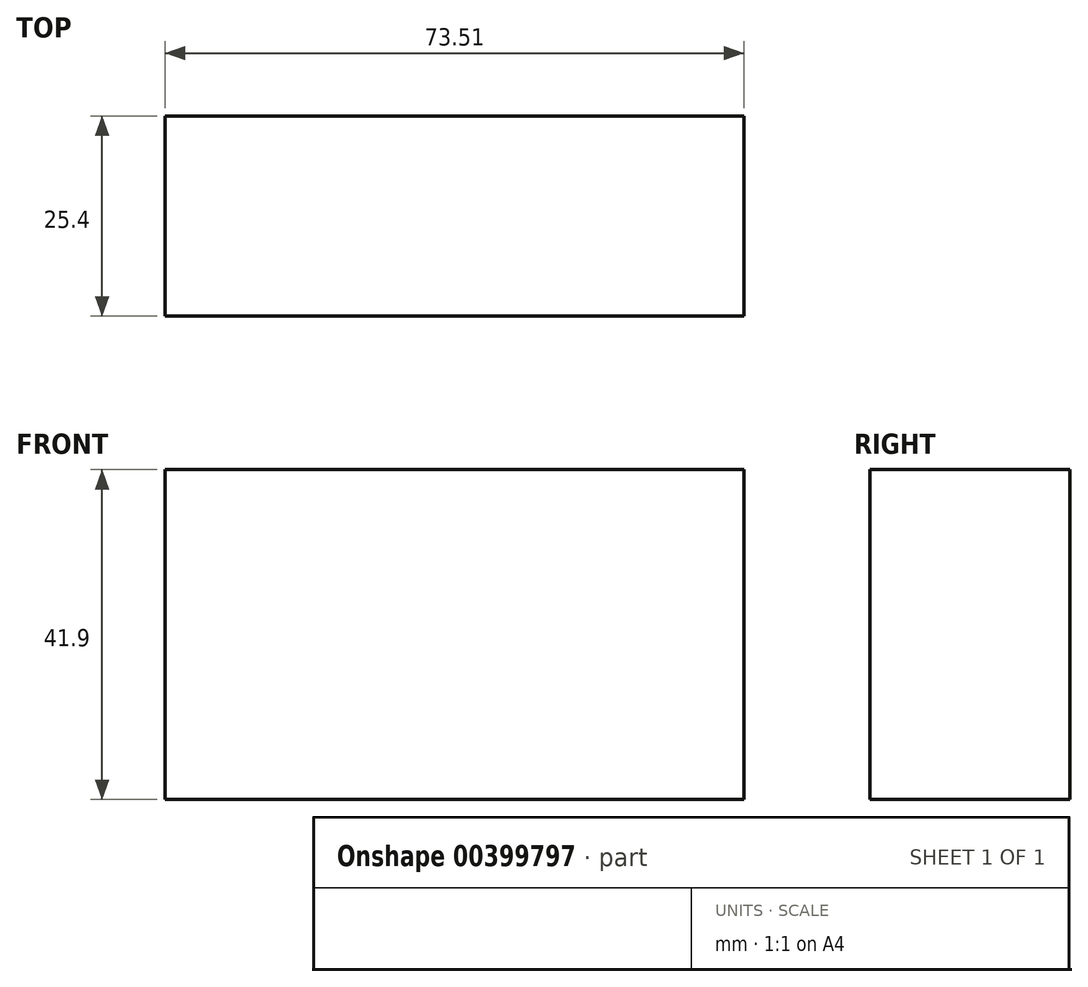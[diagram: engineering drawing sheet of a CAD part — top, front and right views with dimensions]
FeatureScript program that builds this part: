
annotation { "Feature Type Name" : "Feature", "Feature Type Description" : "" }
export const myFeature = defineFeature(function(context is Context, id is Id, definition is map)
    precondition{}
    {
        {
            var Q0;
            Q0=qCreatedBy(makeId("Front.planeOp"),FACE);
            var sketch = newSketch(context, id + "F0", { "sketchPlane" : qUnion([Q0])});
            skLineSegment(sketch, "E0.bottom", {"start": v(-37.63, 21.83) * mm, "end": v(35.88, 21.83) * mm});
            skLineSegment(sketch, "E0.top", {"start": v(-37.63, -20.07) * mm, "end": v(35.88, -20.07) * mm});
            skLineSegment(sketch, "E0.left", {"start": v(-37.63, 21.83) * mm, "end": v(-37.63, -20.07) * mm});
            skLineSegment(sketch, "E0.right", {"start": v(35.88, 21.83) * mm, "end": v(35.88, -20.07) * mm});
            skSolve(sketch);
        }
        {
            var Q0;
            Q0 = qSketchRegion(id + "F0", true);
            extrude(context, id + "F1", {"entities" : qUnion([Q0]), "depth" : 25.4 * mm});
        }
    });
